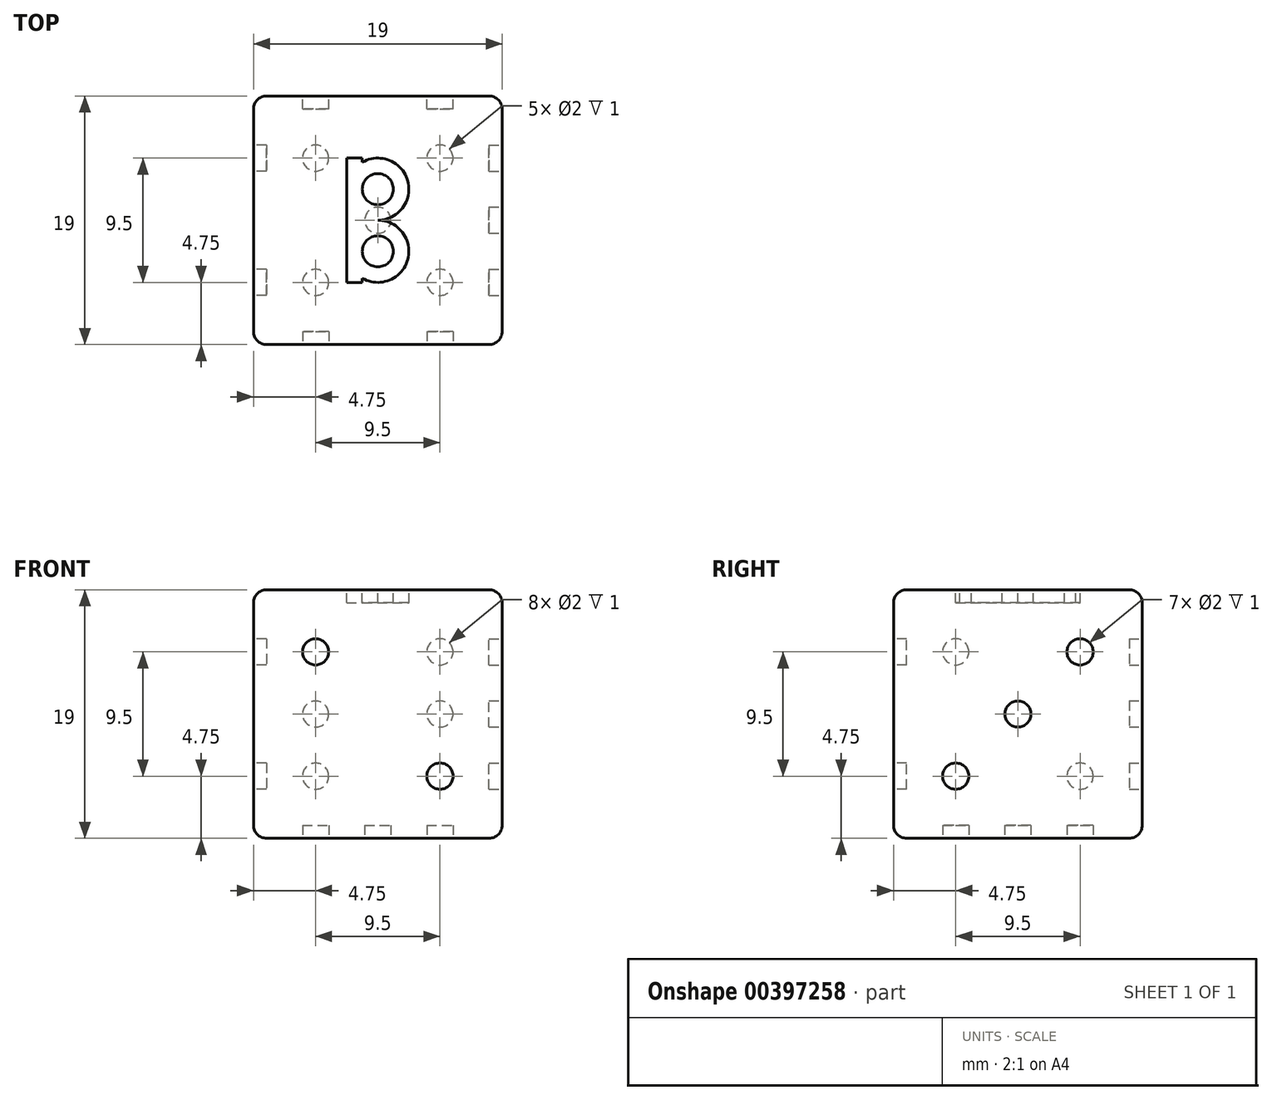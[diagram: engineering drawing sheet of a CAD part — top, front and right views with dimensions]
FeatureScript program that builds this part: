
annotation { "Feature Type Name" : "Feature", "Feature Type Description" : "" }
export const myFeature = defineFeature(function(context is Context, id is Id, definition is map)
    precondition{}
    {
        {
            var Q0;
            Q0=qCreatedBy(makeId("Top.planeOp"),FACE);
            var sketch = newSketch(context, id + "F0", { "sketchPlane" : qUnion([Q0])});
            skLineSegment(sketch, "E0.bottom", {"start": v(0, 0) * mm, "end": v(-19, 0) * mm});
            skLineSegment(sketch, "E0.top", {"start": v(0, 19) * mm, "end": v(-19, 19) * mm});
            skLineSegment(sketch, "E0.left", {"start": v(0, 0) * mm, "end": v(0, 19) * mm});
            skLineSegment(sketch, "E0.right", {"start": v(-19, 0) * mm, "end": v(-19, 19) * mm});
            skSolve(sketch);
        }
        {
            var Q0;
            Q0=makeQuery(id+"F0.imprint","IMPRINT",FACE,{"disambiguationData":[TD([[makeQuery(id+"F0.imprint","IMPRINT",EDGE,{"derivedFrom":sQuery(id+"F0.wireOp",EDGE,"E0.bottom")}),-1.0]])]});
            extrude(context, id + "F1", {"entities" : qUnion([Q0]), "depth" : 19 * mm});
        }
        {
            var Q0;
            Q0=makeQuery(id+"F1.opExtrude","CAP_FACE",FACE,{"disambiguationData":[OSD([sQuery(id+"F0.wireOp",EDGE,"E0.bottom"),sQuery(id+"F0.wireOp",EDGE,"E0.top"),sQuery(id+"F0.wireOp",EDGE,"E0.left"),sQuery(id+"F0.wireOp",EDGE,"E0.right")])],"isStart":false});
            var sketch = newSketch(context, id + "F2", { "sketchPlane" : qUnion([Q0])});
            skLineSegment(sketch, "E1", {"start": v(-9.5, 19) * mm, "end": v(-9.5, 0) * mm, "construction": true});
            skLineSegment(sketch, "E2", {"start": v(-19, 9.5) * mm, "end": v(0, 9.5) * mm, "construction": true});
            skLineSegment(sketch, "E3", {"start": v(-19, 14.25) * mm, "end": v(0, 14.25) * mm, "construction": true});
            skLineSegment(sketch, "E4", {"start": v(-19, 4.75) * mm, "end": v(0, 4.75) * mm, "construction": true});
            skLineSegment(sketch, "E5", {"start": v(-14.25, 19) * mm, "end": v(-14.25, 0) * mm, "construction": true});
            skLineSegment(sketch, "E6", {"start": v(-4.75, 19) * mm, "end": v(-4.75, 0) * mm, "construction": true});
            skPoint(sketch, "E7", {"position": v(-14.25, 14.25) * mm});
            skPoint(sketch, "E8", {"position": v(-4.75, 14.25) * mm});
            skPoint(sketch, "E9", {"position": v(-14.25, 4.75) * mm});
            skPoint(sketch, "E10", {"position": v(-4.75, 4.75) * mm});
            skPoint(sketch, "E11", {"position": v(-9.5, 14.25) * mm});
            skPoint(sketch, "E12", {"position": v(-9.5, 4.75) * mm});
            skPoint(sketch, "E13", {"position": v(-11.87, 14.25) * mm});
            skPoint(sketch, "E14", {"position": v(-7.12, 14.25) * mm});
            skLineSegment(sketch, "E15", {"start": v(-11.87, 14.25) * mm, "end": v(-11.87, 4.75) * mm});
            skLineSegment(sketch, "E16", {"start": v(-7.12, 14.25) * mm, "end": v(-7.12, 4.75) * mm, "construction": true});
            skLineSegment(sketch, "E17", {"start": v(-7.12, 14.25) * mm, "end": v(-11.87, 9.5) * mm, "construction": true});
            skLineSegment(sketch, "E18", {"start": v(-11.87, 14.25) * mm, "end": v(-7.12, 9.5) * mm, "construction": true});
            skLineSegment(sketch, "E19", {"start": v(-11.87, 4.75) * mm, "end": v(-7.12, 9.5) * mm, "construction": true});
            skLineSegment(sketch, "E20", {"start": v(-11.87, 9.5) * mm, "end": v(-7.12, 4.75) * mm, "construction": true});
            skLineSegment(sketch, "E21", {"start": v(-10.69, 14.25) * mm, "end": v(-10.69, 4.75) * mm});
            skCircle(sketch, "E22", {"center": v(-9.5, 11.88) * mm, "radius": 1.19 * mm});
            skCircle(sketch, "E23", {"center": v(-9.5, 11.88) * mm, "radius": 2.38 * mm});
            skCircle(sketch, "E24", {"center": v(-9.5, 7.13) * mm, "radius": 2.38 * mm});
            skCircle(sketch, "E25", {"center": v(-9.5, 7.13) * mm, "radius": 1.19 * mm});
            skLineSegment(sketch, "E26", {"start": v(-11.87, 14.25) * mm, "end": v(-10.69, 14.25) * mm});
            skLineSegment(sketch, "E27", {"start": v(-11.87, 4.75) * mm, "end": v(-10.69, 4.75) * mm});
            skSolve(sketch);
        }
        {
            var Q0;
            {var subQ0=sQuery(id+"F2.wireOp",EDGE,"E23");var subQ1=sQuery(id+"F2.wireOp",EDGE,"E15");var subQ2=makeQuery(id+"F2.imprint","INTERSECT",VERTEX,{"derivedFrom":[subQ1,subQ0]});Q0=makeQuery(id+"F2.imprint","IMPRINT",FACE,{"disambiguationData":[TD([[makeQuery(id+"F2.imprint","IMPRINT",EDGE,{"disambiguationData":[TD([[subQ2,-1.0]])],"derivedFrom":subQ1}),1.0]])]});}
            var Q1;
            {var subQ0=sQuery(id+"F2.wireOp",EDGE,"E21");var subQ1=makeQuery(id+"F2.imprint","INTERSECT",VERTEX,{"derivedFrom":[subQ0,sQuery(id+"F2.wireOp",EDGE,"E22")]});Q1=makeQuery(id+"F2.imprint","IMPRINT",FACE,{"disambiguationData":[TD([[makeQuery(id+"F2.imprint","IMPRINT",EDGE,{"disambiguationData":[TD([[subQ1,1.0]])],"derivedFrom":subQ0}),-1.0]])]});}
            var Q2;
            {var subQ4=sQuery(id+"F2.wireOp",EDGE,"E22");Q2=makeQuery(id+"F2.imprint","IMPRINT",FACE,{"disambiguationData":[TD([[makeQuery(id+"F2.imprint","IMPRINT",EDGE,{"derivedFrom":subQ4}),-1.0]])]});}
            var Q3;
            {var subQ4=sQuery(id+"F2.wireOp",EDGE,"E25");Q3=makeQuery(id+"F2.imprint","IMPRINT",FACE,{"disambiguationData":[TD([[makeQuery(id+"F2.imprint","IMPRINT",EDGE,{"derivedFrom":subQ4}),-1.0]])]});}
            var Q4;
            {var subQ0=sQuery(id+"F2.wireOp",EDGE,"E21");var subQ1=makeQuery(id+"F2.imprint","INTERSECT",VERTEX,{"derivedFrom":[subQ0,sQuery(id+"F2.wireOp",EDGE,"E25")]});Q4=makeQuery(id+"F2.imprint","IMPRINT",FACE,{"disambiguationData":[TD([[makeQuery(id+"F2.imprint","IMPRINT",EDGE,{"disambiguationData":[TD([[subQ1,1.0]])],"derivedFrom":subQ0}),-1.0]])]});}
            var Q5;
            {var subQ0=sQuery(id+"F2.wireOp",EDGE,"E23");var subQ1=sQuery(id+"F2.wireOp",EDGE,"E21");var subQ2=makeQuery(id+"F2.imprint","INTERSECT",VERTEX,{"disambiguationData":[OD(1.0)],"derivedFrom":[subQ1,subQ0]});Q5=makeQuery(id+"F2.imprint","IMPRINT",FACE,{"disambiguationData":[TD([[makeQuery(id+"F2.imprint","IMPRINT",EDGE,{"disambiguationData":[TD([[subQ2,-1.0]])],"derivedFrom":subQ1}),1.0]])]});}
            var Q6;
            {var subQ0=sQuery(id+"F2.wireOp",EDGE,"E27");Q6=makeQuery(id+"F2.imprint","IMPRINT",FACE,{"disambiguationData":[TD([[makeQuery(id+"F2.imprint","IMPRINT",EDGE,{"derivedFrom":subQ0}),1.0]])]});}
            var Q7;
            {var subQ0=sQuery(id+"F2.wireOp",EDGE,"E26");Q7=makeQuery(id+"F2.imprint","IMPRINT",FACE,{"disambiguationData":[TD([[makeQuery(id+"F2.imprint","IMPRINT",EDGE,{"derivedFrom":subQ0}),-1.0]])]});}
            extrude(context, id + "F3", {"entities" : qUnion([Q0, Q1, Q2, Q3, Q4, Q5, Q6, Q7]), "operationType" : NewBodyOperationType.REMOVE, "oppositeDirection" : true, "depth" : 1 * mm});
        }
        {
            var Q0;
            Q0=makeQuery(id+"F1.opExtrude","SWEPT_FACE",FACE,{"disambiguationData":[OSD([sQuery(id+"F0.wireOp",EDGE,"E0.bottom")])]});
            var sketch = newSketch(context, id + "F4", { "sketchPlane" : qUnion([Q0])});
            skPoint(sketch, "E28", {"position": v(-9.5, 19) * mm});
            skPoint(sketch, "E29", {"position": v(-9.5, 0) * mm});
            skPoint(sketch, "E30", {"position": v(-19, 9.5) * mm});
            skPoint(sketch, "E31", {"position": v(0, 9.5) * mm});
            skPoint(sketch, "E32", {"position": v(-14.25, 19) * mm});
            skPoint(sketch, "E33", {"position": v(-4.75, 19) * mm});
            skPoint(sketch, "E34", {"position": v(-19, 14.25) * mm});
            skPoint(sketch, "E35", {"position": v(-19, 4.75) * mm});
            skLineSegment(sketch, "E36", {"start": v(-19, 14.25) * mm, "end": v(0, 14.25) * mm, "construction": true});
            skLineSegment(sketch, "E37", {"start": v(-19, 4.75) * mm, "end": v(0, 4.75) * mm, "construction": true});
            skLineSegment(sketch, "E38", {"start": v(-14.25, 19) * mm, "end": v(-14.25, 0) * mm, "construction": true});
            skLineSegment(sketch, "E39", {"start": v(-4.75, 19) * mm, "end": v(-4.75, 0) * mm, "construction": true});
            skLineSegment(sketch, "E40", {"start": v(-9.5, 19) * mm, "end": v(-9.5, 0) * mm, "construction": true});
            skLineSegment(sketch, "E41", {"start": v(-19, 9.5) * mm, "end": v(0, 9.5) * mm, "construction": true});
            skCircle(sketch, "E42", {"center": v(-14.25, 14.25) * mm, "radius": 1 * mm});
            skCircle(sketch, "E43", {"center": v(-4.75, 4.75) * mm, "radius": 1 * mm});
            skSolve(sketch);
        }
        {
            var Q0;
            Q0=makeQuery(id+"F4.imprint","IMPRINT",FACE,{"disambiguationData":[TD([[makeQuery(id+"F4.imprint","IMPRINT",EDGE,{"derivedFrom":sQuery(id+"F4.wireOp",EDGE,"E42")}),1.0]])]});
            var Q1;
            Q1=makeQuery(id+"F4.imprint","IMPRINT",FACE,{"disambiguationData":[TD([[makeQuery(id+"F4.imprint","IMPRINT",EDGE,{"derivedFrom":sQuery(id+"F4.wireOp",EDGE,"E43")}),1.0]])]});
            extrude(context, id + "F5", {"entities" : qUnion([Q0, Q1]), "operationType" : NewBodyOperationType.REMOVE, "oppositeDirection" : true, "depth" : 1 * mm});
        }
        {
            var Q0;
            Q0=makeQuery(id+"F1.opExtrude","CAP_FACE",FACE,{"disambiguationData":[OSD([sQuery(id+"F0.wireOp",EDGE,"E0.bottom"),sQuery(id+"F0.wireOp",EDGE,"E0.top"),sQuery(id+"F0.wireOp",EDGE,"E0.left"),sQuery(id+"F0.wireOp",EDGE,"E0.right")])],"isStart":true});
            var sketch = newSketch(context, id + "F6", { "sketchPlane" : qUnion([Q0])});
            skLineSegment(sketch, "E44", {"start": v(-9.5, 0) * mm, "end": v(-9.5, -19) * mm, "construction": true});
            skLineSegment(sketch, "E45", {"start": v(-19, -9.5) * mm, "end": v(0, -9.5) * mm, "construction": true});
            skLineSegment(sketch, "E46", {"start": v(-14.25, 0) * mm, "end": v(-14.25, -19) * mm, "construction": true});
            skLineSegment(sketch, "E47", {"start": v(-4.75, 0) * mm, "end": v(-4.75, -19) * mm, "construction": true});
            skLineSegment(sketch, "E48", {"start": v(-19, -4.75) * mm, "end": v(0, -4.75) * mm, "construction": true});
            skLineSegment(sketch, "E49", {"start": v(-19, -14.25) * mm, "end": v(0, -14.25) * mm, "construction": true});
            skCircle(sketch, "E50", {"center": v(-14.25, -4.75) * mm, "radius": 1 * mm});
            skCircle(sketch, "E51", {"center": v(-14.25, -14.25) * mm, "radius": 1 * mm});
            skCircle(sketch, "E52", {"center": v(-4.75, -4.75) * mm, "radius": 1 * mm});
            skCircle(sketch, "E53", {"center": v(-4.75, -14.25) * mm, "radius": 1 * mm});
            skCircle(sketch, "E54", {"center": v(-9.5, -9.5) * mm, "radius": 1 * mm});
            skSolve(sketch);
        }
        {
            var Q0;
            Q0=makeQuery(id+"F6.imprint","IMPRINT",FACE,{"disambiguationData":[TD([[makeQuery(id+"F6.imprint","IMPRINT",EDGE,{"derivedFrom":sQuery(id+"F6.wireOp",EDGE,"E50")}),1.0]])]});
            var Q1;
            Q1=makeQuery(id+"F6.imprint","IMPRINT",FACE,{"disambiguationData":[TD([[makeQuery(id+"F6.imprint","IMPRINT",EDGE,{"derivedFrom":sQuery(id+"F6.wireOp",EDGE,"E54")}),1.0]])]});
            var Q2;
            Q2=makeQuery(id+"F6.imprint","IMPRINT",FACE,{"disambiguationData":[TD([[makeQuery(id+"F6.imprint","IMPRINT",EDGE,{"derivedFrom":sQuery(id+"F6.wireOp",EDGE,"E52")}),1.0]])]});
            var Q3;
            Q3=makeQuery(id+"F6.imprint","IMPRINT",FACE,{"disambiguationData":[TD([[makeQuery(id+"F6.imprint","IMPRINT",EDGE,{"derivedFrom":sQuery(id+"F6.wireOp",EDGE,"E53")}),1.0]])]});
            var Q4;
            Q4=makeQuery(id+"F6.imprint","IMPRINT",FACE,{"disambiguationData":[TD([[makeQuery(id+"F6.imprint","IMPRINT",EDGE,{"derivedFrom":sQuery(id+"F6.wireOp",EDGE,"E51")}),1.0]])]});
            extrude(context, id + "F7", {"entities" : qUnion([Q0, Q1, Q2, Q3, Q4]), "operationType" : NewBodyOperationType.REMOVE, "oppositeDirection" : true, "depth" : 1 * mm});
        }
        {
            var Q0;
            Q0=makeQuery(id+"F1.opExtrude","SWEPT_FACE",FACE,{"disambiguationData":[OSD([sQuery(id+"F0.wireOp",EDGE,"E0.top")])]});
            var sketch = newSketch(context, id + "F8", { "sketchPlane" : qUnion([Q0])});
            skLineSegment(sketch, "E55", {"start": v(9.5, 19) * mm, "end": v(9.5, 0) * mm, "construction": true});
            skLineSegment(sketch, "E56", {"start": v(0, 9.5) * mm, "end": v(19, 9.5) * mm, "construction": true});
            skLineSegment(sketch, "E57", {"start": v(0, 14.25) * mm, "end": v(19, 14.25) * mm, "construction": true});
            skLineSegment(sketch, "E58", {"start": v(0, 4.75) * mm, "end": v(19, 4.75) * mm, "construction": true});
            skLineSegment(sketch, "E59", {"start": v(14.25, 19) * mm, "end": v(14.25, 0) * mm, "construction": true});
            skLineSegment(sketch, "E60", {"start": v(4.75, 19) * mm, "end": v(4.75, 0) * mm, "construction": true});
            skCircle(sketch, "E61", {"center": v(4.75, 14.25) * mm, "radius": 1 * mm});
            skCircle(sketch, "E62", {"center": v(4.75, 9.5) * mm, "radius": 1 * mm});
            skCircle(sketch, "E63", {"center": v(4.75, 4.75) * mm, "radius": 1 * mm});
            skCircle(sketch, "E64", {"center": v(14.25, 14.25) * mm, "radius": 1 * mm});
            skCircle(sketch, "E65", {"center": v(14.25, 9.5) * mm, "radius": 1 * mm});
            skCircle(sketch, "E66", {"center": v(14.25, 4.75) * mm, "radius": 1 * mm});
            skSolve(sketch);
        }
        {
            var Q0;
            Q0=makeQuery(id+"F8.imprint","IMPRINT",FACE,{"disambiguationData":[TD([[makeQuery(id+"F8.imprint","IMPRINT",EDGE,{"derivedFrom":sQuery(id+"F8.wireOp",EDGE,"E61")}),1.0]])]});
            var Q1;
            Q1=makeQuery(id+"F8.imprint","IMPRINT",FACE,{"disambiguationData":[TD([[makeQuery(id+"F8.imprint","IMPRINT",EDGE,{"derivedFrom":sQuery(id+"F8.wireOp",EDGE,"E62")}),1.0]])]});
            var Q2;
            Q2=makeQuery(id+"F8.imprint","IMPRINT",FACE,{"disambiguationData":[TD([[makeQuery(id+"F8.imprint","IMPRINT",EDGE,{"derivedFrom":sQuery(id+"F8.wireOp",EDGE,"E63")}),1.0]])]});
            var Q3;
            Q3=makeQuery(id+"F8.imprint","IMPRINT",FACE,{"disambiguationData":[TD([[makeQuery(id+"F8.imprint","IMPRINT",EDGE,{"derivedFrom":sQuery(id+"F8.wireOp",EDGE,"E66")}),1.0]])]});
            var Q4;
            Q4=makeQuery(id+"F8.imprint","IMPRINT",FACE,{"disambiguationData":[TD([[makeQuery(id+"F8.imprint","IMPRINT",EDGE,{"derivedFrom":sQuery(id+"F8.wireOp",EDGE,"E65")}),1.0]])]});
            var Q5;
            Q5=makeQuery(id+"F8.imprint","IMPRINT",FACE,{"disambiguationData":[TD([[makeQuery(id+"F8.imprint","IMPRINT",EDGE,{"derivedFrom":sQuery(id+"F8.wireOp",EDGE,"E64")}),1.0]])]});
            extrude(context, id + "F9", {"entities" : qUnion([Q0, Q1, Q2, Q3, Q4, Q5]), "operationType" : NewBodyOperationType.REMOVE, "depth" : -1 * mm});
        }
        {
            var Q0;
            Q0=makeQuery(id+"F1.opExtrude","SWEPT_FACE",FACE,{"disambiguationData":[OSD([sQuery(id+"F0.wireOp",EDGE,"E0.left")])]});
            var sketch = newSketch(context, id + "F10", { "sketchPlane" : qUnion([Q0])});
            skLineSegment(sketch, "E67", {"start": v(9.5, 19) * mm, "end": v(9.5, 0) * mm, "construction": true});
            skLineSegment(sketch, "E68", {"start": v(0, 9.5) * mm, "end": v(19, 9.5) * mm, "construction": true});
            skLineSegment(sketch, "E69", {"start": v(4.75, 19) * mm, "end": v(4.75, 0) * mm, "construction": true});
            skLineSegment(sketch, "E70", {"start": v(14.25, 19) * mm, "end": v(14.25, 0) * mm, "construction": true});
            skLineSegment(sketch, "E71", {"start": v(0, 14.25) * mm, "end": v(19, 14.25) * mm, "construction": true});
            skLineSegment(sketch, "E72", {"start": v(0, 4.75) * mm, "end": v(19, 4.75) * mm, "construction": true});
            skCircle(sketch, "E73", {"center": v(4.75, 4.75) * mm, "radius": 1 * mm});
            skCircle(sketch, "E74", {"center": v(9.5, 9.5) * mm, "radius": 1 * mm});
            skCircle(sketch, "E75", {"center": v(14.25, 14.25) * mm, "radius": 1 * mm});
            skSolve(sketch);
        }
        {
            var Q0;
            Q0=makeQuery(id+"F10.imprint","IMPRINT",FACE,{"disambiguationData":[TD([[makeQuery(id+"F10.imprint","IMPRINT",EDGE,{"derivedFrom":sQuery(id+"F10.wireOp",EDGE,"E73")}),1.0]])]});
            var Q1;
            Q1=makeQuery(id+"F10.imprint","IMPRINT",FACE,{"disambiguationData":[TD([[makeQuery(id+"F10.imprint","IMPRINT",EDGE,{"derivedFrom":sQuery(id+"F10.wireOp",EDGE,"E74")}),1.0]])]});
            var Q2;
            Q2=makeQuery(id+"F10.imprint","IMPRINT",FACE,{"disambiguationData":[TD([[makeQuery(id+"F10.imprint","IMPRINT",EDGE,{"derivedFrom":sQuery(id+"F10.wireOp",EDGE,"E75")}),1.0]])]});
            extrude(context, id + "F11", {"entities" : qUnion([Q0, Q1, Q2]), "operationType" : NewBodyOperationType.REMOVE, "oppositeDirection" : true, "depth" : 1 * mm});
        }
        {
            var Q0;
            Q0=makeQuery(id+"F1.opExtrude","SWEPT_FACE",FACE,{"disambiguationData":[OSD([sQuery(id+"F0.wireOp",EDGE,"E0.right")])]});
            var sketch = newSketch(context, id + "F12", { "sketchPlane" : qUnion([Q0])});
            skLineSegment(sketch, "E76", {"start": v(-9.5, 19) * mm, "end": v(-9.5, 0) * mm, "construction": true});
            skLineSegment(sketch, "E77", {"start": v(-19, 9.5) * mm, "end": v(0, 9.5) * mm, "construction": true});
            skLineSegment(sketch, "E78", {"start": v(-4.75, 19) * mm, "end": v(-4.75, 0) * mm, "construction": true});
            skLineSegment(sketch, "E79", {"start": v(-14.25, 19) * mm, "end": v(-14.25, 0) * mm, "construction": true});
            skLineSegment(sketch, "E80", {"start": v(-19, 14.25) * mm, "end": v(0, 14.25) * mm, "construction": true});
            skLineSegment(sketch, "E81", {"start": v(-19, 4.75) * mm, "end": v(0, 4.75) * mm, "construction": true});
            skCircle(sketch, "E82", {"center": v(-14.25, 14.25) * mm, "radius": 1 * mm});
            skCircle(sketch, "E83", {"center": v(-14.25, 4.75) * mm, "radius": 1 * mm});
            skCircle(sketch, "E84", {"center": v(-4.75, 14.25) * mm, "radius": 1 * mm});
            skCircle(sketch, "E85", {"center": v(-4.75, 4.75) * mm, "radius": 1 * mm});
            skSolve(sketch);
        }
        {
            var Q0;
            Q0=makeQuery(id+"F12.imprint","IMPRINT",FACE,{"disambiguationData":[TD([[makeQuery(id+"F12.imprint","IMPRINT",EDGE,{"derivedFrom":sQuery(id+"F12.wireOp",EDGE,"E82")}),1.0]])]});
            var Q1;
            Q1=makeQuery(id+"F12.imprint","IMPRINT",FACE,{"disambiguationData":[TD([[makeQuery(id+"F12.imprint","IMPRINT",EDGE,{"derivedFrom":sQuery(id+"F12.wireOp",EDGE,"E84")}),1.0]])]});
            var Q2;
            Q2=makeQuery(id+"F12.imprint","IMPRINT",FACE,{"disambiguationData":[TD([[makeQuery(id+"F12.imprint","IMPRINT",EDGE,{"derivedFrom":sQuery(id+"F12.wireOp",EDGE,"E83")}),1.0]])]});
            var Q3;
            Q3=makeQuery(id+"F12.imprint","IMPRINT",FACE,{"disambiguationData":[TD([[makeQuery(id+"F12.imprint","IMPRINT",EDGE,{"derivedFrom":sQuery(id+"F12.wireOp",EDGE,"E85")}),1.0]])]});
            extrude(context, id + "F13", {"entities" : qUnion([Q0, Q1, Q2, Q3]), "operationType" : NewBodyOperationType.REMOVE, "oppositeDirection" : true, "depth" : 1 * mm});
        }
        {
            var Q0;
            Q0=makeQuery(id+"F1.opExtrude","CAP_EDGE",EDGE,{"disambiguationData":[OSD([sQuery(id+"F0.wireOp",EDGE,"E0.left")])],"isStart":false});
            var Q1;
            Q1=makeQuery(id+"F1.opExtrude","CAP_EDGE",EDGE,{"disambiguationData":[OSD([sQuery(id+"F0.wireOp",EDGE,"E0.top")])],"isStart":false});
            var Q2;
            Q2=makeQuery(id+"F1.opExtrude","CAP_EDGE",EDGE,{"disambiguationData":[OSD([sQuery(id+"F0.wireOp",EDGE,"E0.bottom")])],"isStart":false});
            var Q3;
            Q3=makeQuery(id+"F1.opExtrude","CAP_EDGE",EDGE,{"disambiguationData":[OSD([sQuery(id+"F0.wireOp",EDGE,"E0.right")])],"isStart":false});
            var Q4;
            Q4=makeQuery(id+"F1.opExtrude","SWEPT_EDGE",EDGE,{"disambiguationData":[OSD([sQuery(id+"F0.wireOp",EDGE,"E0.bottom"),sQuery(id+"F0.wireOp",EDGE,"E0.right")])]});
            var Q5;
            Q5=makeQuery(id+"F1.opExtrude","SWEPT_EDGE",EDGE,{"disambiguationData":[OSD([sQuery(id+"F0.wireOp",EDGE,"E0.top"),sQuery(id+"F0.wireOp",EDGE,"E0.right")])]});
            var Q6;
            Q6=makeQuery(id+"F1.opExtrude","SWEPT_EDGE",EDGE,{"disambiguationData":[OSD([sQuery(id+"F0.wireOp",EDGE,"E0.top"),sQuery(id+"F0.wireOp",EDGE,"E0.left")])]});
            var Q7;
            Q7=makeQuery(id+"F1.opExtrude","SWEPT_EDGE",EDGE,{"disambiguationData":[OSD([sQuery(id+"F0.wireOp",EDGE,"E0.bottom"),sQuery(id+"F0.wireOp",EDGE,"E0.left")])]});
            var Q8;
            Q8=makeQuery(id+"F1.opExtrude","CAP_EDGE",EDGE,{"disambiguationData":[OSD([sQuery(id+"F0.wireOp",EDGE,"E0.bottom")])],"isStart":true});
            var Q9;
            Q9=makeQuery(id+"F1.opExtrude","CAP_EDGE",EDGE,{"disambiguationData":[OSD([sQuery(id+"F0.wireOp",EDGE,"E0.top")])],"isStart":true});
            var Q10;
            Q10=makeQuery(id+"F1.opExtrude","CAP_EDGE",EDGE,{"disambiguationData":[OSD([sQuery(id+"F0.wireOp",EDGE,"E0.right")])],"isStart":true});
            var Q11;
            Q11=makeQuery(id+"F1.opExtrude","CAP_EDGE",EDGE,{"disambiguationData":[OSD([sQuery(id+"F0.wireOp",EDGE,"E0.left")])],"isStart":true});
            fillet(context, id + "F14", {"entities" : qUnion([Q0, Q1, Q2, Q3, Q4, Q5, Q6, Q7, Q8, Q9, Q10, Q11]), "radius" : 1 * mm, "tangentPropagation" : true, "allowEdgeOverflow" : false});
        }
    });
